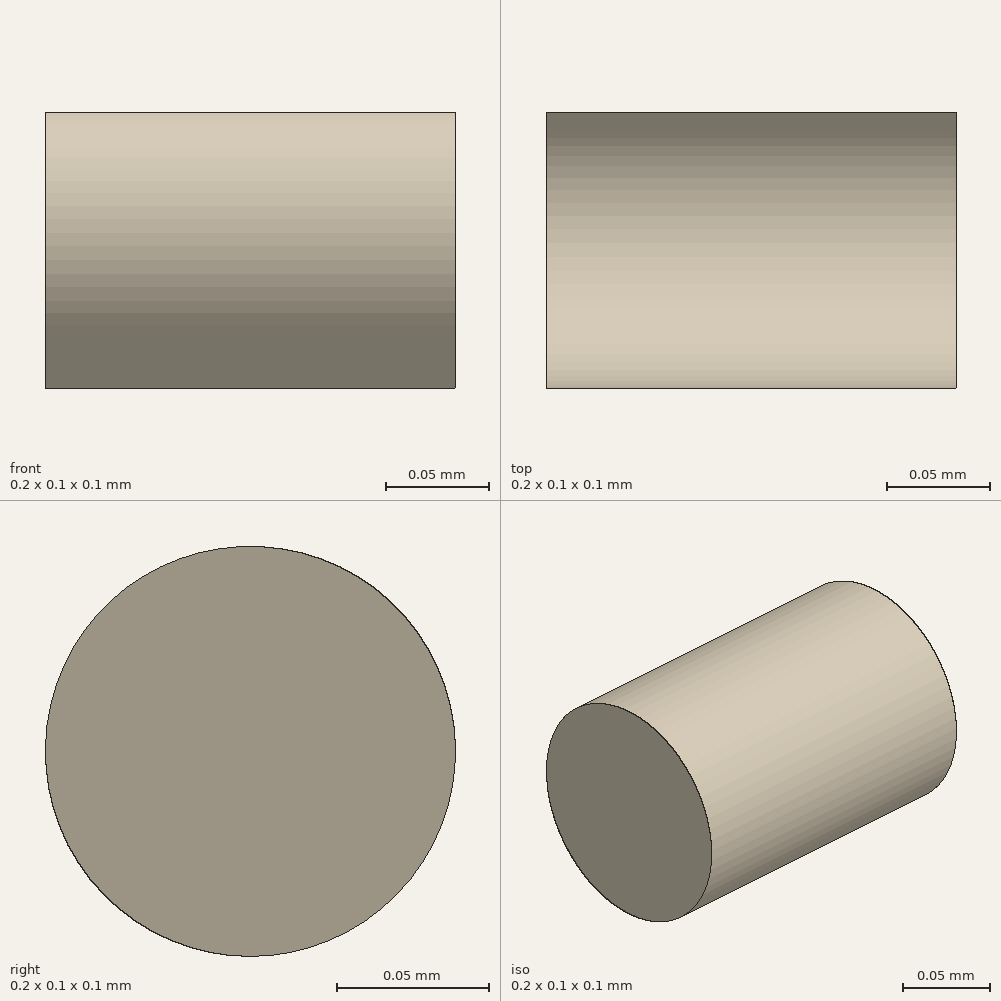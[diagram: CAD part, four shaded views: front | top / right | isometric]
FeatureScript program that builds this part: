
annotation { "Feature Type Name" : "Feature", "Feature Type Description" : "" }
export const myFeature = defineFeature(function(context is Context, id is Id, definition is map)
    precondition{}
    {
        {
            var Q0;
            Q0=qCreatedBy(makeId("Right.planeOp"),FACE);
            var sketch = newSketch(context, id + "F0", { "sketchPlane" : qUnion([Q0])});
            skCircle(sketch, "E0", {"center": v(0, 0) * mm, "radius": 0.07 * mm});
            skSolve(sketch);
        }
        {
            var Q0;
            Q0=qSketchRegion(id+"F0",true);
            extrude(context, id + "F1", {"entities" : qUnion([Q0]), "depth" : 0.2 * mm, "offsetDistance" : 25 * mm});
        }
    });
